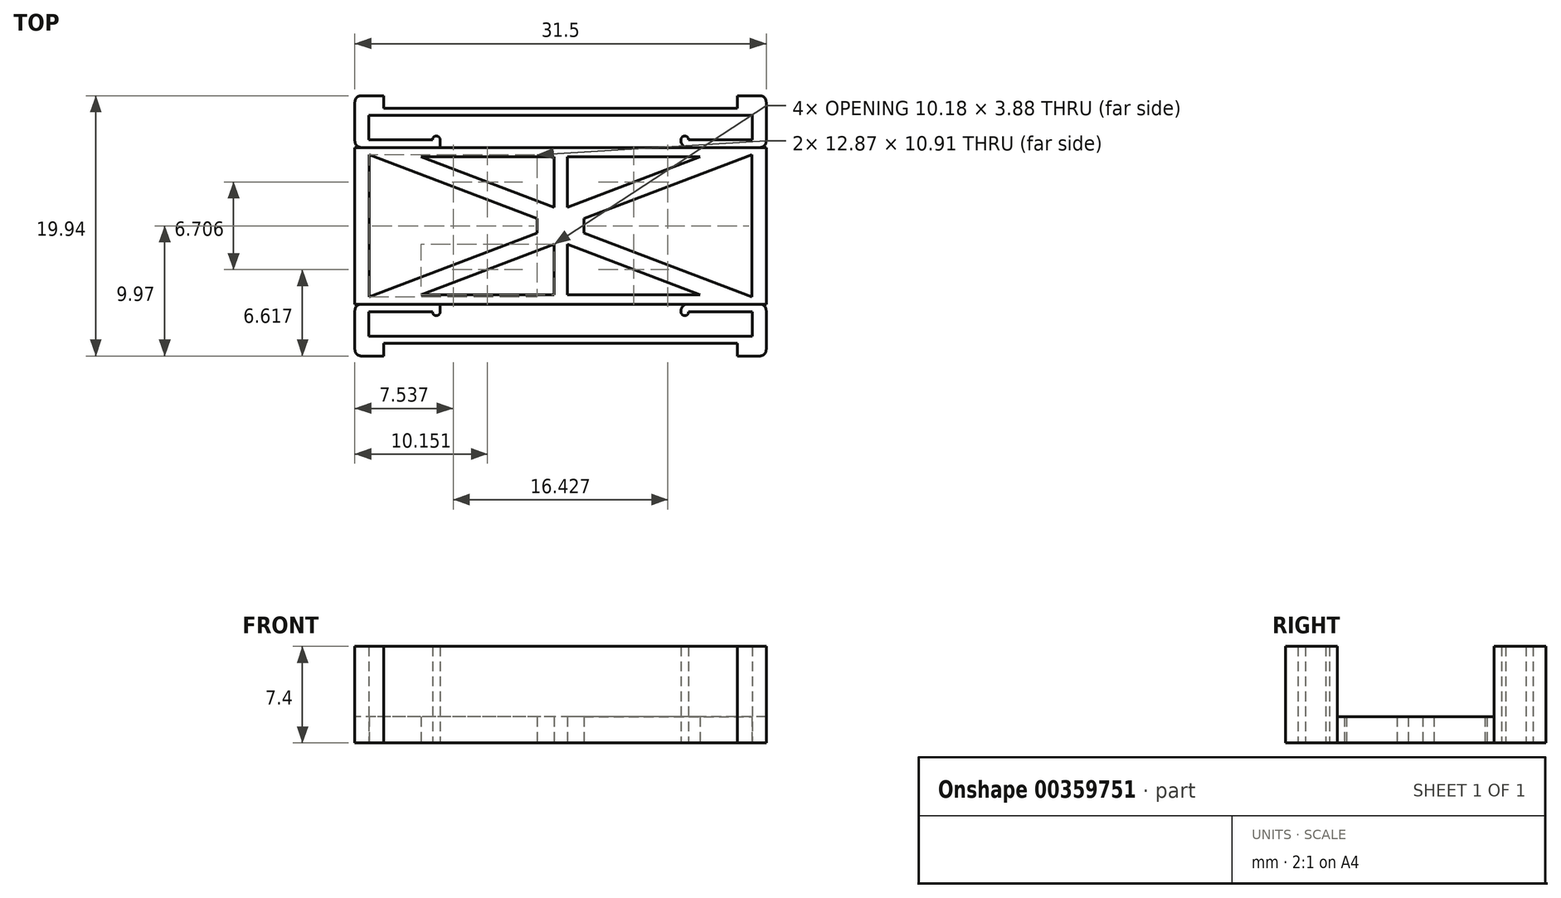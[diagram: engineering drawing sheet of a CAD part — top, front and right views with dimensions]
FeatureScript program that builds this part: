
annotation { "Feature Type Name" : "Feature", "Feature Type Description" : "" }
export const myFeature = defineFeature(function(context is Context, id is Id, definition is map)
    precondition{}
    {
        {
            var Q0;
            Q0=qCreatedBy(makeId("Top.planeOp"),FACE);
            var sketch = newSketch(context, id + "F0", { "sketchPlane" : qUnion([Q0])});
            skPoint(sketch, "E0.middle", {"position": v(0, 0) * mm});
            skLineSegment(sketch, "E1.bottom", {"start": v(13.55, 9) * mm, "end": v(-13.55, 9) * mm});
            skLineSegment(sketch, "E1.top", {"start": v(13.55, -9) * mm, "end": v(-13.55, -9) * mm});
            skLineSegment(sketch, "E1.left", {"start": v(15.75, 9) * mm, "end": v(15.75, -9) * mm});
            skLineSegment(sketch, "E1.right", {"start": v(-15.75, 9) * mm, "end": v(-15.75, -9) * mm});
            skLineSegment(sketch, "E2", {"start": v(15.75, -9) * mm, "end": v(15.75, -9.97) * mm});
            skLineSegment(sketch, "E3", {"start": v(15.75, -9.97) * mm, "end": v(13.55, -9.97) * mm});
            skLineSegment(sketch, "E4", {"start": v(-15.75, -9) * mm, "end": v(-15.75, -9.97) * mm});
            skLineSegment(sketch, "E5", {"start": v(-15.75, -9.97) * mm, "end": v(-13.55, -9.97) * mm});
            skLineSegment(sketch, "E6", {"start": v(-15.75, 9) * mm, "end": v(-15.75, 9.97) * mm});
            skLineSegment(sketch, "E7", {"start": v(-15.75, 9.97) * mm, "end": v(-13.55, 9.97) * mm});
            skLineSegment(sketch, "E8", {"start": v(-13.55, 9.97) * mm, "end": v(-13.55, 9) * mm});
            skLineSegment(sketch, "E9", {"start": v(15.75, 9) * mm, "end": v(15.75, 9.97) * mm});
            skLineSegment(sketch, "E10", {"start": v(15.75, 9.97) * mm, "end": v(13.55, 9.97) * mm});
            skLineSegment(sketch, "E11", {"start": v(-13.55, -9.97) * mm, "end": v(-13.55, -9) * mm});
            skLineSegment(sketch, "E12", {"start": v(13.55, 9.97) * mm, "end": v(13.55, 9) * mm});
            skLineSegment(sketch, "E13", {"start": v(13.55, -9.97) * mm, "end": v(13.55, -9) * mm});
            skLineSegment(sketch, "E14.bottom", {"start": v(15.75, 6) * mm, "end": v(-15.75, 6) * mm});
            skLineSegment(sketch, "E14.top", {"start": v(15.75, -6) * mm, "end": v(-15.75, -6) * mm});
            skLineSegment(sketch, "E14.left", {"start": v(15.75, 6) * mm, "end": v(15.75, -6) * mm});
            skLineSegment(sketch, "E14.right", {"start": v(-15.75, 6) * mm, "end": v(-15.75, -6) * mm});
            skSolve(sketch);
        }
        {
            var Q0;
            Q0=makeQuery(id+"F0.imprint","IMPRINT",FACE,{"disambiguationData":[TD([[makeQuery(id+"F0.imprint","IMPRINT",EDGE,{"derivedFrom":sQuery(id+"F0.wireOp",EDGE,"E1.top")}),-1.0]])]});
            var Q1;
            Q1=makeQuery(id+"F0.imprint","IMPRINT",FACE,{"disambiguationData":[TD([[makeQuery(id+"F0.imprint","IMPRINT",EDGE,{"derivedFrom":sQuery(id+"F0.wireOp",EDGE,"E1.bottom")}),1.0]])]});
            extrude(context, id + "F1", {"entities" : qUnion([Q0, Q1]), "depth" : 7.4 * mm});
        }
        {
            var Q0;
            Q0=makeQuery(id+"F0.imprint","IMPRINT",FACE,{"disambiguationData":[TD([[makeQuery(id+"F0.imprint","IMPRINT",EDGE,{"derivedFrom":sQuery(id+"F0.wireOp",EDGE,"E14.bottom")}),1.0]])]});
            extrude(context, id + "F2", {"entities" : qUnion([Q0]), "depth" : 2 * mm});
        }
        {
            var Q0;
            Q0=makeQuery(id+"F0.imprint","IMPRINT",FACE,{"disambiguationData":[TD([[makeQuery(id+"F0.imprint","IMPRINT",EDGE,{"derivedFrom":sQuery(id+"F0.wireOp",EDGE,"E14.bottom")}),1.0]])]});
            var sketch = newSketch(context, id + "F3", { "sketchPlane" : qUnion([Q0])});
            skPoint(sketch, "E15.0", {"position": v(-15.75, -9) * mm});
            skPoint(sketch, "E15.1", {"position": v(0, 0) * mm});
            skLineSegment(sketch, "E15.2", {"start": v(13.55, 9) * mm, "end": v(-13.55, 9) * mm, "construction": true});
            skLineSegment(sketch, "E15.3", {"start": v(13.55, -9) * mm, "end": v(-13.55, -9) * mm, "construction": true});
            skLineSegment(sketch, "E15.4", {"start": v(15.75, 9) * mm, "end": v(15.75, -9) * mm, "construction": true});
            skLineSegment(sketch, "E15.5", {"start": v(-15.75, 9) * mm, "end": v(-15.75, -9) * mm, "construction": true});
            skPoint(sketch, "E15.6", {"position": v(0, 0) * mm});
            skLineSegment(sketch, "E15.7", {"start": v(15.75, -9) * mm, "end": v(15.75, -9.97) * mm, "construction": true});
            skLineSegment(sketch, "E15.8", {"start": v(15.75, -9.97) * mm, "end": v(13.55, -9.97) * mm, "construction": true});
            skLineSegment(sketch, "E15.9", {"start": v(-15.75, -9) * mm, "end": v(-15.75, -9.97) * mm, "construction": true});
            skLineSegment(sketch, "E15.10", {"start": v(-15.75, -9.97) * mm, "end": v(-13.55, -9.97) * mm, "construction": true});
            skLineSegment(sketch, "E15.11", {"start": v(-15.75, 9) * mm, "end": v(-15.75, 9.97) * mm, "construction": true});
            skLineSegment(sketch, "E15.12", {"start": v(-15.75, 9.97) * mm, "end": v(-13.55, 9.97) * mm, "construction": true});
            skLineSegment(sketch, "E15.13", {"start": v(-13.55, 9.97) * mm, "end": v(-13.55, 9) * mm, "construction": true});
            skLineSegment(sketch, "E15.14", {"start": v(15.75, 9) * mm, "end": v(15.75, 9.97) * mm, "construction": true});
            skLineSegment(sketch, "E15.15", {"start": v(15.75, 9.97) * mm, "end": v(13.55, 9.97) * mm, "construction": true});
            skLineSegment(sketch, "E15.16", {"start": v(-13.55, -9.97) * mm, "end": v(-13.55, -9) * mm, "construction": true});
            skLineSegment(sketch, "E15.17", {"start": v(13.55, 9.97) * mm, "end": v(13.55, 9) * mm, "construction": true});
            skLineSegment(sketch, "E15.18", {"start": v(13.55, -9.97) * mm, "end": v(13.55, -9) * mm, "construction": true});
            skLineSegment(sketch, "E15.21", {"start": v(15.75, 6) * mm, "end": v(15.75, -6) * mm});
            skLineSegment(sketch, "E15.22", {"start": v(-15.75, 6) * mm, "end": v(-15.75, -6) * mm});
            skPoint(sketch, "E15.23", {"position": v(0, 0) * mm});
            skLineSegment(sketch, "E16", {"start": v(-15.75, -6) * mm, "end": v(15.75, 6) * mm, "construction": true});
            skLineSegment(sketch, "E17", {"start": v(15.75, -6) * mm, "end": v(-15.75, 6) * mm, "construction": true});
            skLineSegment(sketch, "E18", {"start": v(-10.7, -5.3) * mm, "end": v(-0.5, -1.41) * mm});
            skLineSegment(sketch, "E19", {"start": v(0.5, -1.41) * mm, "end": v(10.7, -5.3) * mm});
            skLineSegment(sketch, "E20", {"start": v(10.7, -5.3) * mm, "end": v(0.5, -5.3) * mm});
            skLineSegment(sketch, "E21", {"start": v(0, -9) * mm, "end": v(0, 9) * mm, "construction": true});
            skLineSegment(sketch, "E22", {"start": v(-15.75, 0) * mm, "end": v(15.75, 0) * mm, "construction": true});
            skLineSegment(sketch, "E23.MirrorCS", {"start": v(10.7, 5.3) * mm, "end": v(0.5, 5.3) * mm});
            skLineSegment(sketch, "E24.MirrorCS", {"start": v(-10.7, 5.3) * mm, "end": v(-0.5, 1.41) * mm});
            skLineSegment(sketch, "E25.MirrorCS", {"start": v(0.5, 1.41) * mm, "end": v(10.7, 5.3) * mm});
            skLineSegment(sketch, "E26.MirrorCS", {"start": v(-13.77, 8.45) * mm, "end": v(-14.68, 8.45) * mm});
            skLineSegment(sketch, "E27.MirrorCS", {"start": v(-7.4, 8.45) * mm, "end": v(-13.08, 8.45) * mm});
            skLineSegment(sketch, "E28.MirrorCS", {"start": v(-13.08, 6.6) * mm, "end": v(-9.8, 6.6) * mm});
            skLineSegment(sketch, "E29.MirrorCS", {"start": v(-14.68, 8.45) * mm, "end": v(-14.68, 6.6) * mm});
            skLineSegment(sketch, "E30.MirrorCS", {"start": v(-14.68, 6.6) * mm, "end": v(-13.77, 6.6) * mm});
            skLineSegment(sketch, "E31", {"start": v(14.65, -5.45) * mm, "end": v(1.78, -0.55) * mm});
            skLineSegment(sketch, "E32", {"start": v(14.65, -0.55) * mm, "end": v(14.65, -5.45) * mm});
            skLineSegment(sketch, "E33.MirrorCS", {"start": v(14.65, 0.55) * mm, "end": v(14.65, 5.45) * mm});
            skLineSegment(sketch, "E34.MirrorCS", {"start": v(14.65, 5.45) * mm, "end": v(1.78, 0.55) * mm});
            skLineSegment(sketch, "E35.MirrorCS", {"start": v(-14.65, 0.55) * mm, "end": v(-14.65, 5.45) * mm});
            skLineSegment(sketch, "E36.MirrorCS", {"start": v(-14.65, 5.45) * mm, "end": v(-1.78, 0.55) * mm});
            skLineSegment(sketch, "E37.MirrorCS", {"start": v(-14.65, -5.45) * mm, "end": v(-1.78, -0.55) * mm});
            skLineSegment(sketch, "E38.MirrorCS", {"start": v(-14.65, -0.55) * mm, "end": v(-14.65, -5.45) * mm});
            skLineSegment(sketch, "E39", {"start": v(-0.5, -5.3) * mm, "end": v(-0.5, -1.41) * mm});
            skLineSegment(sketch, "E40.MirrorCS", {"start": v(0.5, -5.3) * mm, "end": v(0.5, -1.41) * mm});
            skLineSegment(sketch, "E41.MirrorCS", {"start": v(0.5, 5.3) * mm, "end": v(0.5, 1.41) * mm});
            skLineSegment(sketch, "E42.MirrorCS", {"start": v(-0.5, 5.3) * mm, "end": v(-0.5, 1.41) * mm});
            skPoint(sketch, "E43.orphan", {"position": v(0, -1.22) * mm});
            skPoint(sketch, "E44.orphan", {"position": v(0, 1.22) * mm});
            skLineSegment(sketch, "E45.trimOffspring", {"start": v(-0.5, 5.3) * mm, "end": v(-10.7, 5.3) * mm});
            skLineSegment(sketch, "E46", {"start": v(-0.5, -5.3) * mm, "end": v(-10.7, -5.3) * mm});
            skLineSegment(sketch, "E47", {"start": v(-13.77, 8.45) * mm, "end": v(-13.08, 8.45) * mm});
            skLineSegment(sketch, "E48", {"start": v(-13.08, 6.6) * mm, "end": v(-13.77, 6.6) * mm});
            skLineSegment(sketch, "E49.MirrorCS", {"start": v(7.4, 8.45) * mm, "end": v(13.08, 8.45) * mm});
            skLineSegment(sketch, "E50.MirrorCS", {"start": v(13.08, 6.6) * mm, "end": v(13.77, 6.6) * mm});
            skLineSegment(sketch, "E51.MirrorCS", {"start": v(13.77, 8.45) * mm, "end": v(14.68, 8.45) * mm});
            skLineSegment(sketch, "E52.MirrorCS", {"start": v(14.68, 6.6) * mm, "end": v(13.77, 6.6) * mm});
            skLineSegment(sketch, "E53.MirrorCS", {"start": v(13.77, 8.45) * mm, "end": v(13.08, 8.45) * mm});
            skLineSegment(sketch, "E54.MirrorCS", {"start": v(14.68, 8.45) * mm, "end": v(14.68, 6.6) * mm});
            skLineSegment(sketch, "E55.MirrorCS", {"start": v(13.08, 6.6) * mm, "end": v(9.8, 6.6) * mm});
            skLineSegment(sketch, "E56.MirrorCS", {"start": v(13.08, -6.6) * mm, "end": v(13.77, -6.6) * mm});
            skLineSegment(sketch, "E57.MirrorCS", {"start": v(13.08, -6.6) * mm, "end": v(9.8, -6.6) * mm});
            skLineSegment(sketch, "E58.MirrorCS", {"start": v(-14.68, -8.45) * mm, "end": v(-14.68, -6.6) * mm});
            skLineSegment(sketch, "E59.MirrorCS", {"start": v(-14.68, -6.6) * mm, "end": v(-13.77, -6.6) * mm});
            skLineSegment(sketch, "E60.MirrorCS", {"start": v(-13.77, -8.45) * mm, "end": v(-13.08, -8.45) * mm});
            skLineSegment(sketch, "E61.MirrorCS", {"start": v(-13.08, -6.6) * mm, "end": v(-13.77, -6.6) * mm});
            skLineSegment(sketch, "E62.MirrorCS", {"start": v(-7.4, -8.45) * mm, "end": v(-13.08, -8.45) * mm});
            skLineSegment(sketch, "E63.MirrorCS", {"start": v(14.68, -8.45) * mm, "end": v(14.68, -6.6) * mm});
            skLineSegment(sketch, "E64.MirrorCS", {"start": v(-13.77, -8.45) * mm, "end": v(-14.68, -8.45) * mm});
            skLineSegment(sketch, "E65.MirrorCS", {"start": v(14.68, -6.6) * mm, "end": v(13.77, -6.6) * mm});
            skLineSegment(sketch, "E66.MirrorCS", {"start": v(-13.08, -6.6) * mm, "end": v(-9.8, -6.6) * mm});
            skLineSegment(sketch, "E67.MirrorCS", {"start": v(13.77, -8.45) * mm, "end": v(14.68, -8.45) * mm});
            skLineSegment(sketch, "E68.MirrorCS", {"start": v(13.77, -8.45) * mm, "end": v(13.08, -8.45) * mm});
            skLineSegment(sketch, "E69.MirrorCS", {"start": v(7.4, -8.45) * mm, "end": v(13.08, -8.45) * mm});
            skLineSegment(sketch, "E70", {"start": v(-6.83, 8.45) * mm, "end": v(6.83, 8.45) * mm});
            skLineSegment(sketch, "E71", {"start": v(9.22, 6.6) * mm, "end": v(9.22, 6) * mm});
            skLineSegment(sketch, "E72", {"start": v(9.22, 6) * mm, "end": v(-9.22, 6) * mm});
            skLineSegment(sketch, "E73", {"start": v(-9.22, 6) * mm, "end": v(-9.22, 6.6) * mm});
            skLineSegment(sketch, "E74", {"start": v(-6.83, -8.45) * mm, "end": v(6.83, -8.45) * mm});
            skLineSegment(sketch, "E75", {"start": v(9.22, -6.6) * mm, "end": v(9.22, -6) * mm});
            skLineSegment(sketch, "E76", {"start": v(9.22, -6) * mm, "end": v(-9.22, -6) * mm});
            skLineSegment(sketch, "E77", {"start": v(-9.22, -6) * mm, "end": v(-9.22, -6.6) * mm});
            skLineSegment(sketch, "E78", {"start": v(-14.65, 0.55) * mm, "end": v(-14.65, -0.55) * mm});
            skLineSegment(sketch, "E79", {"start": v(-1.78, 0.55) * mm, "end": v(-1.78, -0.55) * mm});
            skLineSegment(sketch, "E80", {"start": v(1.78, 0.55) * mm, "end": v(1.78, -0.55) * mm});
            skLineSegment(sketch, "E81", {"start": v(14.65, 0.55) * mm, "end": v(14.65, -0.55) * mm});
            skLineSegment(sketch, "E82", {"start": v(-7.4, -8.45) * mm, "end": v(-6.83, -8.45) * mm});
            skLineSegment(sketch, "E83", {"start": v(6.83, -8.45) * mm, "end": v(7.4, -8.45) * mm});
            skLineSegment(sketch, "E84", {"start": v(7.4, 8.45) * mm, "end": v(6.83, 8.45) * mm});
            skLineSegment(sketch, "E85", {"start": v(-7.4, 8.45) * mm, "end": v(-6.83, 8.45) * mm});
            skArc(sketch, "E86", {"start": v(-9.22, 6.6) * mm, "mid": v(-9.51, 6.88) * mm, "end": v(-9.8, 6.6) * mm});
            skArc(sketch, "E87.MirrorCS", {"start": v(9.22, 6.6) * mm, "mid": v(9.51, 6.88) * mm, "end": v(9.8, 6.6) * mm});
            skArc(sketch, "E88.MirrorCS", {"start": v(9.22, -6.6) * mm, "mid": v(9.51, -6.88) * mm, "end": v(9.8, -6.6) * mm});
            skArc(sketch, "E89.MirrorCS", {"start": v(-9.22, -6.6) * mm, "mid": v(-9.51, -6.88) * mm, "end": v(-9.8, -6.6) * mm});
            skSolve(sketch);
        }
        {
            var Q0;
            Q0=makeQuery(id+"F3.imprint","IMPRINT",FACE,{"disambiguationData":[TD([[makeQuery(id+"F3.imprint","IMPRINT",EDGE,{"derivedFrom":sQuery(id+"F3.wireOp",EDGE,"c9262d61-5d93-4ecc-ac70-7c9b4b996b403.MirrorCS")}),1.0]])]});
            var Q1;
            Q1=makeQuery(id+"F3.imprint","IMPRINT",FACE,{"disambiguationData":[TD([[makeQuery(id+"F3.imprint","IMPRINT",EDGE,{"derivedFrom":sQuery(id+"F3.wireOp",EDGE,"E18")}),-1.0]])]});
            var Q2;
            Q2=makeQuery(id+"F3.imprint","IMPRINT",FACE,{"disambiguationData":[TD([[makeQuery(id+"F3.imprint","IMPRINT",EDGE,{"derivedFrom":sQuery(id+"F3.wireOp",EDGE,"E19")}),-1.0]])]});
            var Q3;
            Q3=makeQuery(id+"F3.imprint","IMPRINT",FACE,{"disambiguationData":[TD([[makeQuery(id+"F3.imprint","IMPRINT",EDGE,{"derivedFrom":sQuery(id+"F3.wireOp",EDGE,"E31")}),-1.0]])]});
            var Q4;
            Q4=makeQuery(id+"F3.imprint","IMPRINT",FACE,{"disambiguationData":[TD([[makeQuery(id+"F3.imprint","IMPRINT",EDGE,{"derivedFrom":sQuery(id+"F3.wireOp",EDGE,"39032eb7-041b-4bfd-afca-cfd52f063a690.MirrorCS")}),1.0]])]});
            var Q5;
            Q5=makeQuery(id+"F3.imprint","IMPRINT",FACE,{"disambiguationData":[TD([[makeQuery(id+"F3.imprint","IMPRINT",EDGE,{"derivedFrom":sQuery(id+"F3.wireOp",EDGE,"E23.MirrorCS")}),1.0]])]});
            var Q6;
            Q6=makeQuery(id+"F3.imprint","IMPRINT",FACE,{"disambiguationData":[TD([[makeQuery(id+"F3.imprint","IMPRINT",EDGE,{"derivedFrom":sQuery(id+"F3.wireOp",EDGE,"E24.MirrorCS")}),1.0]])]});
            var Q7;
            Q7=makeQuery(id+"F3.imprint","IMPRINT",FACE,{"disambiguationData":[TD([[makeQuery(id+"F3.imprint","IMPRINT",EDGE,{"derivedFrom":sQuery(id+"F3.wireOp",EDGE,"E26.MirrorCS")}),1.0]])]});
            var Q8;
            Q8=makeQuery(id+"F3.imprint","IMPRINT",FACE,{"disambiguationData":[TD([[makeQuery(id+"F3.imprint","IMPRINT",EDGE,{"derivedFrom":sQuery(id+"F3.wireOp",EDGE,"ad9057ef-bf56-415d-aac9-48c9a5eaa9f96.MirrorCS")}),1.0]])]});
            var Q9;
            Q9=makeQuery(id+"F3.imprint","IMPRINT",FACE,{"disambiguationData":[TD([[makeQuery(id+"F3.imprint","IMPRINT",EDGE,{"derivedFrom":sQuery(id+"F3.wireOp",EDGE,"ad9057ef-bf56-415d-aac9-48c9a5eaa9f97.MirrorCS")}),-1.0]])]});
            var Q10;
            Q10=makeQuery(id+"F3.imprint","IMPRINT",FACE,{"disambiguationData":[TD([[makeQuery(id+"F3.imprint","IMPRINT",EDGE,{"derivedFrom":sQuery(id+"F3.wireOp",EDGE,"ad9057ef-bf56-415d-aac9-48c9a5eaa9f93.MirrorCS")}),1.0]])]});
            var Q11;
            Q11=makeQuery(id+"F3.imprint","IMPRINT",FACE,{"disambiguationData":[TD([[makeQuery(id+"F3.imprint","IMPRINT",EDGE,{"derivedFrom":sQuery(id+"F3.wireOp",EDGE,"ad9057ef-bf56-415d-aac9-48c9a5eaa9f99.MirrorCS")}),-1.0]])]});
            var Q12;
            Q12=makeQuery(id+"F3.imprint","IMPRINT",FACE,{"disambiguationData":[TD([[makeQuery(id+"F3.imprint","IMPRINT",EDGE,{"derivedFrom":sQuery(id+"F3.wireOp",EDGE,"ad9057ef-bf56-415d-aac9-48c9a5eaa9f98.MirrorCS")}),-1.0]])]});
            var Q13;
            Q13=makeQuery(id+"F3.imprint","IMPRINT",FACE,{"disambiguationData":[TD([[makeQuery(id+"F3.imprint","IMPRINT",EDGE,{"derivedFrom":sQuery(id+"F3.wireOp",EDGE,"4f6b49aa-7395-4091-8d25-70588253103c0.MirrorCS")}),1.0]])]});
            var Q14;
            Q14=makeQuery(id+"F3.imprint","IMPRINT",FACE,{"disambiguationData":[TD([[makeQuery(id+"F3.imprint","IMPRINT",EDGE,{"derivedFrom":sQuery(id+"F3.wireOp",EDGE,"4f6b49aa-7395-4091-8d25-70588253103c1.MirrorCS")}),1.0]])]});
            var Q15;
            Q15=makeQuery(id+"F3.imprint","IMPRINT",FACE,{"disambiguationData":[TD([[makeQuery(id+"F3.imprint","IMPRINT",EDGE,{"derivedFrom":sQuery(id+"F3.wireOp",EDGE,"4f6b49aa-7395-4091-8d25-70588253103c2.MirrorCS")}),1.0]])]});
            var Q16;
            Q16=makeQuery(id+"F3.imprint","IMPRINT",FACE,{"disambiguationData":[TD([[makeQuery(id+"F3.imprint","IMPRINT",EDGE,{"derivedFrom":sQuery(id+"F3.wireOp",EDGE,"x4lQ23kr-62zK-1eZt-kRhK-krumElUWfU3l.bottom")}),-1.0]])]});
            var Q17;
            Q17=makeQuery(id+"F3.imprint","IMPRINT",FACE,{"disambiguationData":[TD([[makeQuery(id+"F3.imprint","IMPRINT",EDGE,{"derivedFrom":sQuery(id+"F3.wireOp",EDGE,"EBCUwdxx-Fegh-ZNc0-f7h1-0w8UD6G6JYo5")}),-1.0]])]});
            var Q18;
            Q18=makeQuery(id+"F3.imprint","IMPRINT",FACE,{"disambiguationData":[TD([[makeQuery(id+"F3.imprint","IMPRINT",EDGE,{"derivedFrom":sQuery(id+"F3.wireOp",EDGE,"JlxLU4ag-6HPh-fue0-Fd91-5WRHmkeVKkq2")}),-1.0]])]});
            var Q19;
            Q19=makeQuery(id+"F3.imprint","IMPRINT",FACE,{"disambiguationData":[TD([[makeQuery(id+"F3.imprint","IMPRINT",EDGE,{"derivedFrom":sQuery(id+"F3.wireOp",EDGE,"E35.MirrorCS")}),-1.0]])]});
            var Q20;
            Q20=makeQuery(id+"F3.imprint","IMPRINT",FACE,{"disambiguationData":[TD([[makeQuery(id+"F3.imprint","IMPRINT",EDGE,{"derivedFrom":sQuery(id+"F3.wireOp",EDGE,"E56.MirrorCS")}),-1.0]])]});
            var Q21;
            Q21=makeQuery(id+"F3.imprint","IMPRINT",FACE,{"disambiguationData":[TD([[makeQuery(id+"F3.imprint","IMPRINT",EDGE,{"derivedFrom":sQuery(id+"F3.wireOp",EDGE,"E49.MirrorCS")}),-1.0]])]});
            var Q22;
            Q22=makeQuery(id+"F3.imprint","IMPRINT",FACE,{"disambiguationData":[TD([[makeQuery(id+"F3.imprint","IMPRINT",EDGE,{"derivedFrom":sQuery(id+"F3.wireOp",EDGE,"HunaMQI0-OEA1-PTBx-195u-SweMD4NwWXyc")}),1.0]])]});
            var Q23;
            Q23=makeQuery(id+"F3.imprint","IMPRINT",FACE,{"disambiguationData":[TD([[makeQuery(id+"F3.imprint","IMPRINT",EDGE,{"derivedFrom":sQuery(id+"F3.wireOp",EDGE,"18fe0dc2-960b-4c37-97ad-dd64be25d0f26.MirrorCS")}),-1.0]])]});
            var Q24;
            Q24=makeQuery(id+"F3.imprint","IMPRINT",FACE,{"disambiguationData":[TD([[makeQuery(id+"F3.imprint","IMPRINT",EDGE,{"derivedFrom":sQuery(id+"F3.wireOp",EDGE,"E58.MirrorCS")}),-1.0]])]});
            extrude(context, id + "F4", {"entities" : qUnion([Q0, Q1, Q2, Q3, Q4, Q5, Q6, Q7, Q8, Q9, Q10, Q11, Q12, Q13, Q14, Q15, Q16, Q17, Q18, Q19, Q20, Q21, Q22, Q23, Q24]), "operationType" : NewBodyOperationType.REMOVE, "depth" : 25 * mm});
        }
        {
            var Q0;
            Q0=makeQuery(id+"F1.opExtrude","SWEPT_EDGE",EDGE,{"disambiguationData":[OSD([sQuery(id+"F0.wireOp",EDGE,"E1.right"),sQuery(id+"F0.wireOp",EDGE,"E14.bottom"),sQuery(id+"F0.wireOp",EDGE,"E14.right")])]});
            var Q1;
            Q1=makeQuery(id+"F1.opExtrude","SWEPT_EDGE",EDGE,{"disambiguationData":[OSD([sQuery(id+"F0.wireOp",EDGE,"E1.right"),sQuery(id+"F0.wireOp",EDGE,"E14.top"),sQuery(id+"F0.wireOp",EDGE,"E14.right")])]});
            var Q2;
            Q2=makeQuery(id+"F1.opExtrude","SWEPT_EDGE",EDGE,{"disambiguationData":[OSD([sQuery(id+"F0.wireOp",EDGE,"E1.left"),sQuery(id+"F0.wireOp",EDGE,"E14.bottom"),sQuery(id+"F0.wireOp",EDGE,"E14.left")])]});
            var Q3;
            Q3=makeQuery(id+"F1.opExtrude","SWEPT_EDGE",EDGE,{"disambiguationData":[OSD([sQuery(id+"F0.wireOp",EDGE,"E1.left"),sQuery(id+"F0.wireOp",EDGE,"E14.top"),sQuery(id+"F0.wireOp",EDGE,"E14.left")])]});
            var Q4;
            Q4=makeQuery(id+"F1.opExtrude","SWEPT_EDGE",EDGE,{"disambiguationData":[OSD([sQuery(id+"F0.wireOp",EDGE,"E2"),sQuery(id+"F0.wireOp",EDGE,"E3")])]});
            var Q5;
            Q5=makeQuery(id+"F1.opExtrude","SWEPT_EDGE",EDGE,{"disambiguationData":[OSD([sQuery(id+"F0.wireOp",EDGE,"E4"),sQuery(id+"F0.wireOp",EDGE,"E5")])]});
            var Q6;
            Q6=makeQuery(id+"F1.opExtrude","SWEPT_EDGE",EDGE,{"disambiguationData":[OSD([sQuery(id+"F0.wireOp",EDGE,"E6"),sQuery(id+"F0.wireOp",EDGE,"E7")])]});
            var Q7;
            Q7=makeQuery(id+"F1.opExtrude","SWEPT_EDGE",EDGE,{"disambiguationData":[OSD([sQuery(id+"F0.wireOp",EDGE,"E9"),sQuery(id+"F0.wireOp",EDGE,"E10")])]});
            fillet(context, id + "F5", {"entities" : qUnion([Q0, Q1, Q2, Q3, Q4, Q5, Q6, Q7]), "radius" : .5 * mm, "tangentPropagation" : true, "allowEdgeOverflow" : false});
        }
        {
            var Q0;
            {var subQ0=sQuery(id+"F0.wireOp",EDGE,"E14.bottom");var subQ1=sQuery(id+"F3.wireOp",EDGE,"E73");Q0=makeQuery(id+"F4.boolean.opBoolean","COPY",EDGE,{"disambiguationData":[topologyDisambiguationEdgeConnected([makeQuery(id+"F1.opExtrude","SWEPT_FACE",FACE,{"disambiguationData":[OSD([subQ0])]})])],"derivedFrom":makeQuery(id+"F4.opExtrude","SWEPT_EDGE",EDGE,{"disambiguationData":[OSD([subQ0,sQuery(id+"F3.wireOp",EDGE,"E72"),subQ1])]})});}
            var Q1;
            {var subQ0=sQuery(id+"F0.wireOp",EDGE,"E14.bottom");var subQ1=sQuery(id+"F3.wireOp",EDGE,"E71");Q1=makeQuery(id+"F4.boolean.opBoolean","COPY",EDGE,{"disambiguationData":[topologyDisambiguationEdgeConnected([makeQuery(id+"F1.opExtrude","SWEPT_FACE",FACE,{"disambiguationData":[OSD([subQ0])]})])],"derivedFrom":makeQuery(id+"F4.opExtrude","SWEPT_EDGE",EDGE,{"disambiguationData":[OSD([subQ0,subQ1,sQuery(id+"F3.wireOp",EDGE,"E72")])]})});}
            var Q2;
            {var subQ0=sQuery(id+"F0.wireOp",EDGE,"E14.top");var subQ1=sQuery(id+"F3.wireOp",EDGE,"E75");Q2=makeQuery(id+"F4.boolean.opBoolean","COPY",EDGE,{"disambiguationData":[topologyDisambiguationEdgeConnected([makeQuery(id+"F1.opExtrude","SWEPT_FACE",FACE,{"disambiguationData":[OSD([subQ0])]})])],"derivedFrom":makeQuery(id+"F4.opExtrude","SWEPT_EDGE",EDGE,{"disambiguationData":[OSD([subQ0,subQ1,sQuery(id+"F3.wireOp",EDGE,"E76")])]})});}
            var Q3;
            {var subQ0=sQuery(id+"F0.wireOp",EDGE,"E14.top");var subQ1=sQuery(id+"F3.wireOp",EDGE,"E77");Q3=makeQuery(id+"F4.boolean.opBoolean","COPY",EDGE,{"disambiguationData":[topologyDisambiguationEdgeConnected([makeQuery(id+"F1.opExtrude","SWEPT_FACE",FACE,{"disambiguationData":[OSD([subQ0])]})])],"derivedFrom":makeQuery(id+"F4.opExtrude","SWEPT_EDGE",EDGE,{"disambiguationData":[OSD([subQ0,sQuery(id+"F3.wireOp",EDGE,"E76"),subQ1])]})});}
            fillet(context, id + "F6", {"entities" : qUnion([Q0, Q1, Q2, Q3]), "radius" : .5 * mm, "tangentPropagation" : true, "allowEdgeOverflow" : false});
        }
    });
